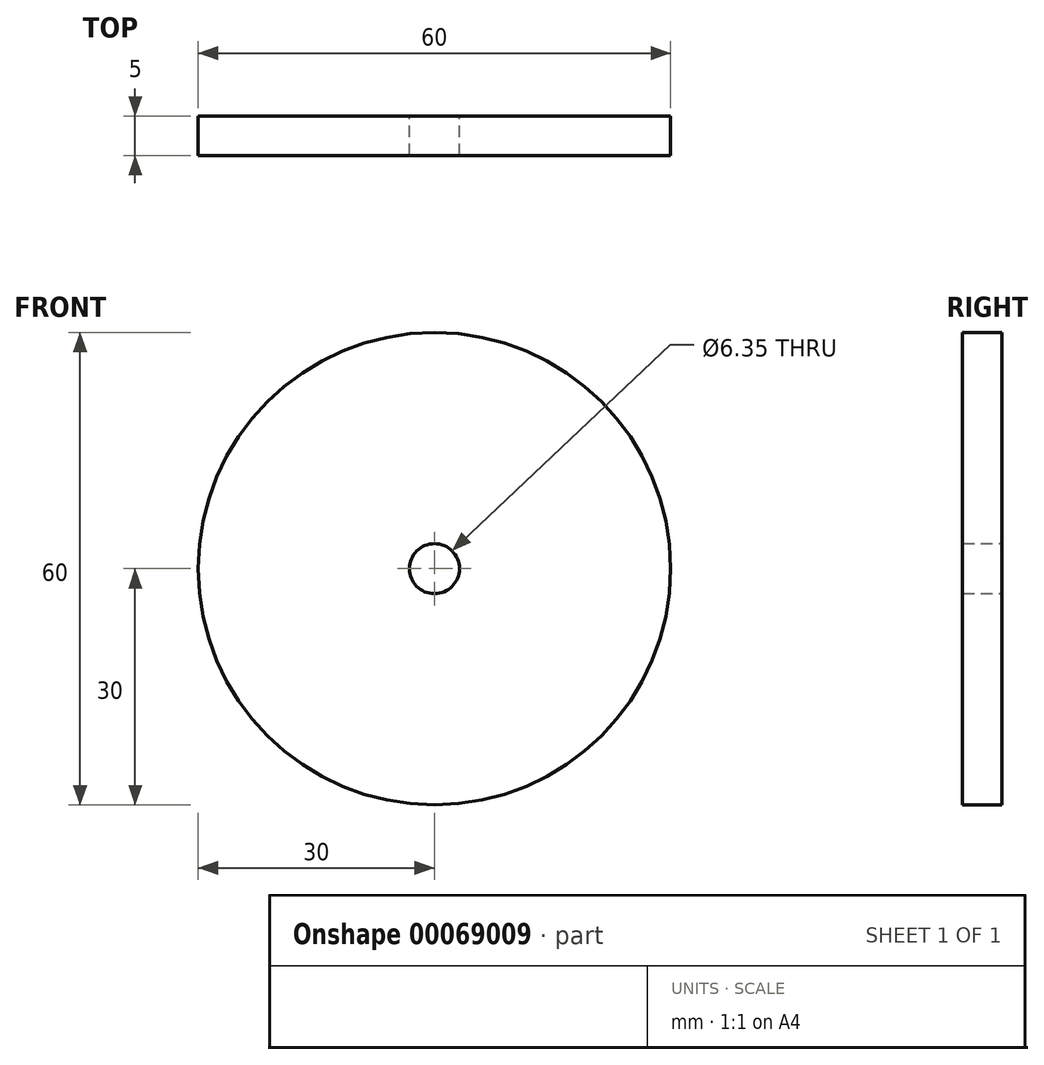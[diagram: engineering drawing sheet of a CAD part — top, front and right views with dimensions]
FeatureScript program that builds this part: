
annotation { "Feature Type Name" : "Feature", "Feature Type Description" : "" }
export const myFeature = defineFeature(function(context is Context, id is Id, definition is map)
    precondition{}
    {
        {
            var Q0;
            Q0=qCreatedBy(makeId("Front.planeOp"),FACE);
            var sketch = newSketch(context, id + "F0", { "sketchPlane" : qUnion([Q0])});
            skCircle(sketch, "E0", {"center": v(0, 0) * mm, "radius": 30 * mm});
            skCircle(sketch, "E1", {"center": v(0, 0) * mm, "radius": 3.17 * mm});
            skSolve(sketch);
        }
        {
            var Q0;
            Q0=makeQuery(id+"F0.imprint","IMPRINT",FACE,{"disambiguationData":[TD([[makeQuery(id+"F0.imprint","IMPRINT",EDGE,{"derivedFrom":sQuery(id+"F0.wireOp",EDGE,"E0")}),1.0]])]});
            extrude(context, id + "F1", {"entities" : qUnion([Q0]), "depth" : 5 * mm});
        }
    });
